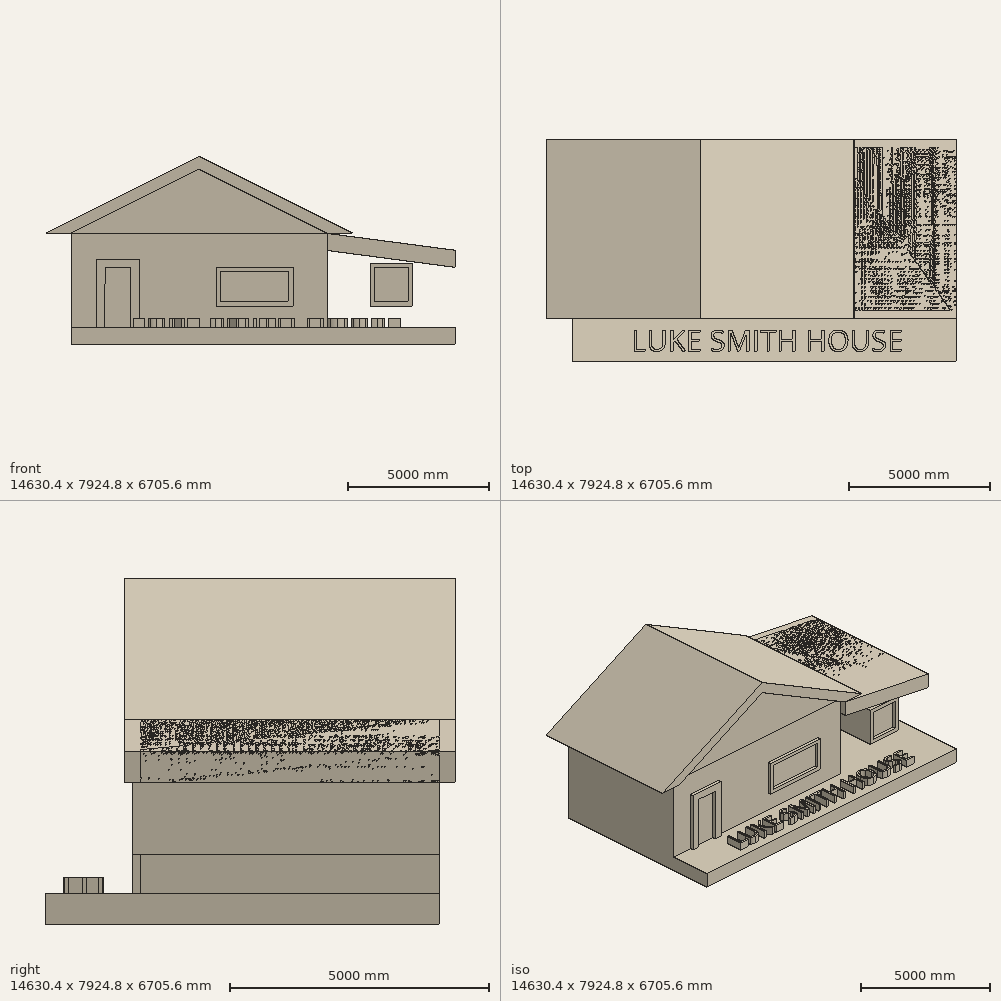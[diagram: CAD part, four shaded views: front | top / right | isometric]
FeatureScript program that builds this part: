
annotation { "Feature Type Name" : "Feature", "Feature Type Description" : "" }
export const myFeature = defineFeature(function(context is Context, id is Id, definition is map)
    precondition{}
    {
        {
            var Q0;
            Q0=qCreatedBy(makeId("Front.planeOp"),FACE);
            var sketch = newSketch(context, id + "F0", { "sketchPlane" : qUnion([Q0])});
            skLineSegment(sketch, "E0", {"start": v(0, 0) * mm, "end": v(-4572, 0) * mm});
            skLineSegment(sketch, "E1", {"start": v(0, 0) * mm, "end": v(4572, 0) * mm});
            skLineSegment(sketch, "E2", {"start": v(0, 0) * mm, "end": v(0, 2286) * mm, "construction": true});
            skLineSegment(sketch, "E3", {"start": v(-4572, 0) * mm, "end": v(0, 2286) * mm});
            skLineSegment(sketch, "E4", {"start": v(0, 2286) * mm, "end": v(4572, 0) * mm});
            skLineSegment(sketch, "E5", {"start": v(-4572, 0) * mm, "end": v(-4572, -3352.8) * mm});
            skLineSegment(sketch, "E6", {"start": v(4572, 0) * mm, "end": v(4572, -3352.8) * mm});
            skLineSegment(sketch, "E7", {"start": v(-4572, -3352.8) * mm, "end": v(4572, -3352.8) * mm});
            skText(sketch, "E8", { "text": "luke smith", "fontName": "OpenSans-Regular.ttf"});
            skLineSegment(sketch, "E9", {"start": v(0, 2286) * mm, "end": v(0, 2743.2) * mm, "construction": true});
            skLineSegment(sketch, "E10", {"start": v(-4572, 0) * mm, "end": v(-5486.4, 0) * mm});
            skLineSegment(sketch, "E11", {"start": v(-5486.4, 0) * mm, "end": v(0, 2743.2) * mm});
            skLineSegment(sketch, "E12", {"start": v(4572, 0) * mm, "end": v(5486.4, 0) * mm});
            skLineSegment(sketch, "E13", {"start": v(5486.4, 0) * mm, "end": v(0, 2743.2) * mm});
            skLineSegment(sketch, "E14", {"start": v(-4572, -3352.8) * mm, "end": v(-4572, -3962.4) * mm});
            skLineSegment(sketch, "E15", {"start": v(4572, -3352.8) * mm, "end": v(4572, -3962.4) * mm});
            skLineSegment(sketch, "E16", {"start": v(-4572, -3962.4) * mm, "end": v(4572, -3962.4) * mm});
            skLineSegment(sketch, "E17", {"start": v(4572, -3352.8) * mm, "end": v(9144, -3352.8) * mm});
            skLineSegment(sketch, "E18", {"start": v(9144, -3352.8) * mm, "end": v(9144, -603.23) * mm});
            skLineSegment(sketch, "E19", {"start": v(9144, -603.23) * mm, "end": v(4572, 0) * mm});
            skLineSegment(sketch, "E20", {"start": v(4572, -3962.4) * mm, "end": v(9144, -3962.4) * mm});
            skLineSegment(sketch, "E21", {"start": v(9144, -3352.8) * mm, "end": v(9144, -3962.4) * mm});
            skLineSegment(sketch, "E22", {"start": v(4572, 0) * mm, "end": v(4572, -609.6) * mm});
            skLineSegment(sketch, "E23", {"start": v(4572, -609.6) * mm, "end": v(9144, -1212.83) * mm});
            skLineSegment(sketch, "E24", {"start": v(6096, -2590.8) * mm, "end": v(6096, -1066.8) * mm});
            skLineSegment(sketch, "E25", {"start": v(6096, -1066.8) * mm, "end": v(7620, -1066.8) * mm});
            skLineSegment(sketch, "E26", {"start": v(7620, -1066.8) * mm, "end": v(7620, -2590.8) * mm});
            skLineSegment(sketch, "E27", {"start": v(7620, -2590.8) * mm, "end": v(6096, -2590.8) * mm});
            skLineSegment(sketch, "E28.bottom", {"start": v(6248.4, -2438.4) * mm, "end": v(7467.6, -2438.4) * mm});
            skLineSegment(sketch, "E28.top", {"start": v(6248.4, -1219.2) * mm, "end": v(7467.6, -1219.2) * mm});
            skLineSegment(sketch, "E28.left", {"start": v(6248.4, -2438.4) * mm, "end": v(6248.4, -1219.2) * mm});
            skLineSegment(sketch, "E28.right", {"start": v(7467.6, -2438.4) * mm, "end": v(7467.6, -1219.2) * mm});
            skLineSegment(sketch, "E29", {"start": v(3352.8, -2590.8) * mm, "end": v(3352.8, -1219.2) * mm});
            skLineSegment(sketch, "E30", {"start": v(3352.8, -2590.8) * mm, "end": v(609.6, -2590.8) * mm});
            skLineSegment(sketch, "E31", {"start": v(609.6, -2590.8) * mm, "end": v(609.6, -1219.2) * mm});
            skLineSegment(sketch, "E32", {"start": v(609.6, -1219.2) * mm, "end": v(3352.8, -1219.2) * mm});
            skLineSegment(sketch, "E33", {"start": v(762, -2438.4) * mm, "end": v(762, -1356.59) * mm});
            skLineSegment(sketch, "E34", {"start": v(3200.4, -1356.59) * mm, "end": v(762, -1356.59) * mm});
            skLineSegment(sketch, "E35", {"start": v(762, -2438.4) * mm, "end": v(3200.4, -2438.4) * mm});
            skLineSegment(sketch, "E36", {"start": v(3200.4, -2438.4) * mm, "end": v(3200.4, -1356.59) * mm});
            skLineSegment(sketch, "E37", {"start": v(-3352.66, -1203.24) * mm, "end": v(-3390.19, -3352.8) * mm});
            skLineSegment(sketch, "E38", {"start": v(-3352.66, -1203.24) * mm, "end": v(-2438.4, -1219.2) * mm});
            skLineSegment(sketch, "E39", {"start": v(-2438.4, -1219.2) * mm, "end": v(-2438.4, -3352.8) * mm});
            skLineSegment(sketch, "E40", {"start": v(-3390.19, -3352.8) * mm, "end": v(-2438.4, -3352.8) * mm});
            skLineSegment(sketch, "E41", {"start": v(-2133.6, -3352.8) * mm, "end": v(-2133.6, -914.4) * mm});
            skLineSegment(sketch, "E42", {"start": v(-3657.6, -3352.8) * mm, "end": v(-3657.6, -914.4) * mm});
            skLineSegment(sketch, "E43", {"start": v(-3657.6, -914.4) * mm, "end": v(-2133.6, -914.4) * mm});
            const initialGuessF0  = {"E8": [-4.22054, 1.78638, 1, 0, 0.30206]};
            skSetInitialGuess(sketch, initialGuessF0);
            skSolve(sketch);
        }
        {
            var Q0;
            Q0=makeQuery(id+"F0.imprint","IMPRINT",FACE,{"disambiguationData":[TD([[makeQuery(id+"F0.imprint","IMPRINT",EDGE,{"derivedFrom":sQuery(id+"F0.wireOp",EDGE,"E3")}),1.0]])]});
            extrude(context, id + "F1", {"entities" : qUnion([Q0]), "depth" : 6096 * mm, "offsetDistance" : 30.48 * mm, "hasSecondDirection" : true, "secondDirectionOppositeDirection" : true, "secondDirectionDepth" : 304.8 * mm});
        }
        {
            var Q0;
            Q0=makeQuery(id+"F0.imprint","IMPRINT",FACE,{"disambiguationData":[TD([[makeQuery(id+"F0.imprint","IMPRINT",EDGE,{"derivedFrom":sQuery(id+"F0.wireOp",EDGE,"E0")}),-1.0]])]});
            extrude(context, id + "F2", {"entities" : qUnion([Q0]), "operationType" : NewBodyOperationType.ADD, "depth" : 5791.2 * mm, "offsetDistance" : 30.48 * mm});
        }
        {
            var Q0;
            {var subQ0=sQuery(id+"F0.wireOp",EDGE,"E19");Q0=makeQuery(id+"F0.imprint","IMPRINT",FACE,{"disambiguationData":[TD([[makeQuery(id+"F0.imprint","IMPRINT",EDGE,{"derivedFrom":subQ0}),1.0]])]});}
            extrude(context, id + "F3", {"entities" : qUnion([Q0]), "depth" : 6096 * mm, "offsetDistance" : 30.48 * mm, "hasSecondDirection" : true, "secondDirectionOppositeDirection" : true, "secondDirectionDepth" : 304.8 * mm});
        }
        {
            var Q0;
            Q0=makeQuery(id+"F0.imprint","IMPRINT",FACE,{"disambiguationData":[TD([[makeQuery(id+"F0.imprint","IMPRINT",EDGE,{"derivedFrom":sQuery(id+"F0.wireOp",EDGE,"E0")}),1.0]])]});
            var Q1;
            Q1=makeQuery(id+"F0.imprint","IMPRINT",FACE,{"disambiguationData":[TD([[makeQuery(id+"F0.imprint","IMPRINT",EDGE,{"derivedFrom":sQuery(id+"F0.wireOp",EDGE,"E6")}),1.0]])]});
            extrude(context, id + "F4", {"entities" : qUnion([Q0, Q1]), "depth" : 5791.2 * mm, "offsetDistance" : 30.48 * mm});
        }
        {
            var Q0;
            {var subQ0=sQuery(id+"F0.wireOp",EDGE,"E37");Q0=makeQuery(id+"F0.imprint","IMPRINT",FACE,{"disambiguationData":[TD([[makeQuery(id+"F0.imprint","IMPRINT",EDGE,{"derivedFrom":subQ0}),-1.0]])]});}
            extrude(context, id + "F5", {"entities" : qUnion([Q0]), "operationType" : NewBodyOperationType.ADD, "depth" : 5943.6 * mm, "offsetDistance" : 30.48 * mm});
        }
        {
            var Q0;
            Q0=makeQuery(id+"F0.imprint","IMPRINT",FACE,{"disambiguationData":[TD([[makeQuery(id+"F0.imprint","IMPRINT",EDGE,{"derivedFrom":sQuery(id+"F0.wireOp",EDGE,"E37")}),1.0]])]});
            extrude(context, id + "F6", {"entities" : qUnion([Q0]), "operationType" : NewBodyOperationType.ADD, "depth" : 5791.2 * mm, "offsetDistance" : 30.48 * mm});
        }
        {
            var Q0;
            Q0=makeQuery(id+"F0.imprint","IMPRINT",FACE,{"disambiguationData":[TD([[makeQuery(id+"F0.imprint","IMPRINT",EDGE,{"derivedFrom":sQuery(id+"F0.wireOp",EDGE,"E29")}),1.0]])]});
            var Q1;
            Q1=makeQuery(id+"F0.imprint","IMPRINT",FACE,{"disambiguationData":[TD([[makeQuery(id+"F0.imprint","IMPRINT",EDGE,{"derivedFrom":sQuery(id+"F0.wireOp",EDGE,"E24")}),-1.0]])]});
            extrude(context, id + "F7", {"entities" : qUnion([Q0, Q1]), "operationType" : NewBodyOperationType.ADD, "depth" : 5943.6 * mm, "offsetDistance" : 30.48 * mm});
        }
        {
            var Q0;
            Q0=makeQuery(id+"F0.imprint","IMPRINT",FACE,{"disambiguationData":[TD([[makeQuery(id+"F0.imprint","IMPRINT",EDGE,{"derivedFrom":sQuery(id+"F0.wireOp",EDGE,"E33")}),-1.0]])]});
            var Q1;
            Q1=makeQuery(id+"F0.imprint","IMPRINT",FACE,{"disambiguationData":[TD([[makeQuery(id+"F0.imprint","IMPRINT",EDGE,{"derivedFrom":sQuery(id+"F0.wireOp",EDGE,"E28.bottom")}),1.0]])]});
            extrude(context, id + "F8", {"entities" : qUnion([Q0, Q1]), "operationType" : NewBodyOperationType.ADD, "depth" : 5791.2 * mm, "offsetDistance" : 30.48 * mm});
        }
        {
            var Q0;
            {var subQ5=sQuery(id+"F0.wireOp",EDGE,"E14");Q0=makeQuery(id+"F0.imprint","IMPRINT",FACE,{"disambiguationData":[TD([[makeQuery(id+"F0.imprint","IMPRINT",EDGE,{"derivedFrom":subQ5}),1.0]])]});}
            var Q1;
            Q1=makeQuery(id+"F0.imprint","IMPRINT",FACE,{"disambiguationData":[TD([[makeQuery(id+"F0.imprint","IMPRINT",EDGE,{"derivedFrom":sQuery(id+"F0.wireOp",EDGE,"E15")}),1.0]])]});
            extrude(context, id + "F9", {"entities" : qUnion([Q0, Q1]), "operationType" : NewBodyOperationType.ADD, "depth" : 7620 * mm, "offsetDistance" : 30.48 * mm});
        }
        {
            var Q0;
            Q0=makeQuery(id+"F9.opExtrude","SWEPT_FACE",FACE,{"disambiguationData":[OSD([sQuery(id+"F0.wireOp",EDGE,"E7"),sQuery(id+"F0.wireOp",EDGE,"E17"),sQuery(id+"F0.wireOp",EDGE,"E40")])]});
            var sketch = newSketch(context, id + "F10", { "sketchPlane" : qUnion([Q0])});
            skText(sketch, "E44", { "text": "LUKE SMITH HOUSE", "fontName": "OpenSans-Regular.ttf"});
            const initialGuessF10  = {"E44": [-2.45685, -7.25504, 1, 0, 0.75077]};
            skSetInitialGuess(sketch, initialGuessF10);
            skSolve(sketch);
        }
        {
            var Q0;
            Q0 = qSketchRegion(id + "F10", true);
            extrude(context, id + "F11", {"entities" : qUnion([Q0]), "operationType" : NewBodyOperationType.ADD, "depth" : 304.8 * mm, "offsetDistance" : 30.48 * mm});
        }
    });
